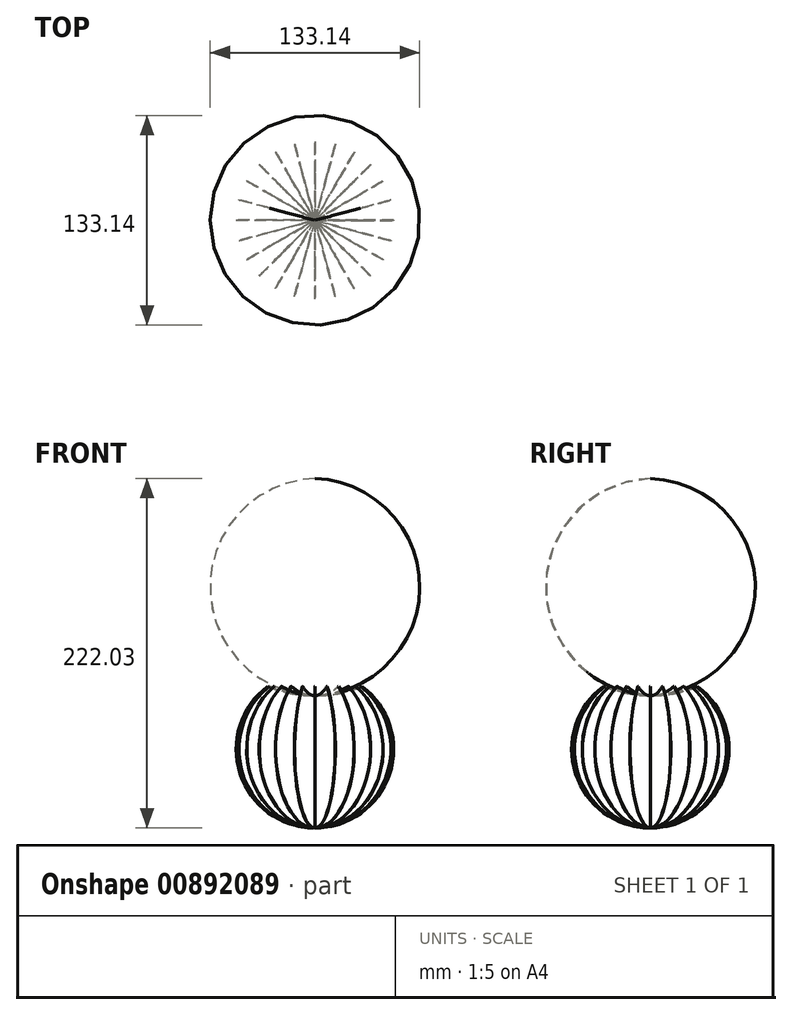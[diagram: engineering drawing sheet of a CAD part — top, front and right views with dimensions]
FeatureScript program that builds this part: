
annotation { "Feature Type Name" : "Feature", "Feature Type Description" : "" }
export const myFeature = defineFeature(function(context is Context, id is Id, definition is map)
    precondition{}
    {
        {
            var Q0;
            Q0=qCreatedBy(makeId("Front.planeOp"),FACE);
            cPlane(context, id + "F0", {"entities" : qUnion([Q0]), "cplaneType" : CPlaneType.OFFSET, "offset" : 0 * mm, "width" : 152.4 * mm, "height" : 152.4 * mm});
        }
        {
            var Q0;
            Q0=qCreatedBy(id+"F0.planeOp",FACE);
            var sketch = newSketch(context, id + "F1", { "sketchPlane" : qUnion([Q0])});
            skLineSegment(sketch, "E0", {"start": v(0, 50) * mm, "end": v(0, -50) * mm});
            skArc(sketch, "E1", {"start": v(0, 50) * mm, "mid": v(-50, 0) * mm, "end": v(0, -50) * mm});
            skSolve(sketch);
        }
        {
            var Q0;
            Q0 = qSketchRegion(id + "F1", true);
            extrude(context, id + "F2", {"entities" : qUnion([Q0]), "endBound" : BoundingType.SYMMETRIC, "depth" : 0.1 * mm, "offsetDistance" : 25 * mm});
        }
        {
            var Q0;
            Q0=makeQuery(id+"F2.opExtrude","SWEPT_BODY",BODY,{"disambiguationData":[OSD([sQuery(id+"F1.wireOp",EDGE,"E0"),sQuery(id+"F1.wireOp",EDGE,"E1")])]});
            var Q1;
            Q1=makeQuery(id+"F2.opExtrude","CAP_EDGE",EDGE,{"disambiguationData":[OSD([sQuery(id+"F1.wireOp",EDGE,"E0")])],"isStart":false});
            circularPattern(context, id + "F3", {"entities" : qUnion([Q0]), "axis" : qUnion([Q1]), "angle" : 360 * degree, "instanceCount" : 24, "equalSpace" : true});
        }
        {
            var Q0;
            Q0=qCreatedBy(id+"F0.planeOp",FACE);
            var sketch = newSketch(context, id + "F4", { "sketchPlane" : qUnion([Q0])});
            skLineSegment(sketch, "E2", {"start": v(0, 34.28) * mm, "end": v(0, 60.23) * mm});
            skLineSegment(sketch, "E3", {"start": v(0, 60.23) * mm, "end": v(56.26, 60.23) * mm});
            skArc(sketch, "E4", {"start": v(0, 34.28) * mm, "mid": v(31.2, 40.58) * mm, "end": v(56.26, 60.23) * mm});
            skSolve(sketch);
        }
        {
            var Q0;
            Q0=makeQuery(id+"F4.imprint","IMPRINT",FACE,{"disambiguationData":[TD([[makeQuery(id+"F4.imprint","IMPRINT",EDGE,{"derivedFrom":sQuery(id+"F4.wireOp",EDGE,"E2")}),-1.0]])]});
            var Q1;
            Q1=sQuery(id+"F4.wireOp",EDGE,"E2");
            revolve(context, id + "F5", {"operationType" : NewBodyOperationType.REMOVE, "surfaceOperationType" : NewSurfaceOperationType.NEW, "entities" : qUnion([Q0]), "axis" : qUnion([Q1]), "revolveType" : RevolveType.FULL, "oppositeDirection" : true});
        }
    });
